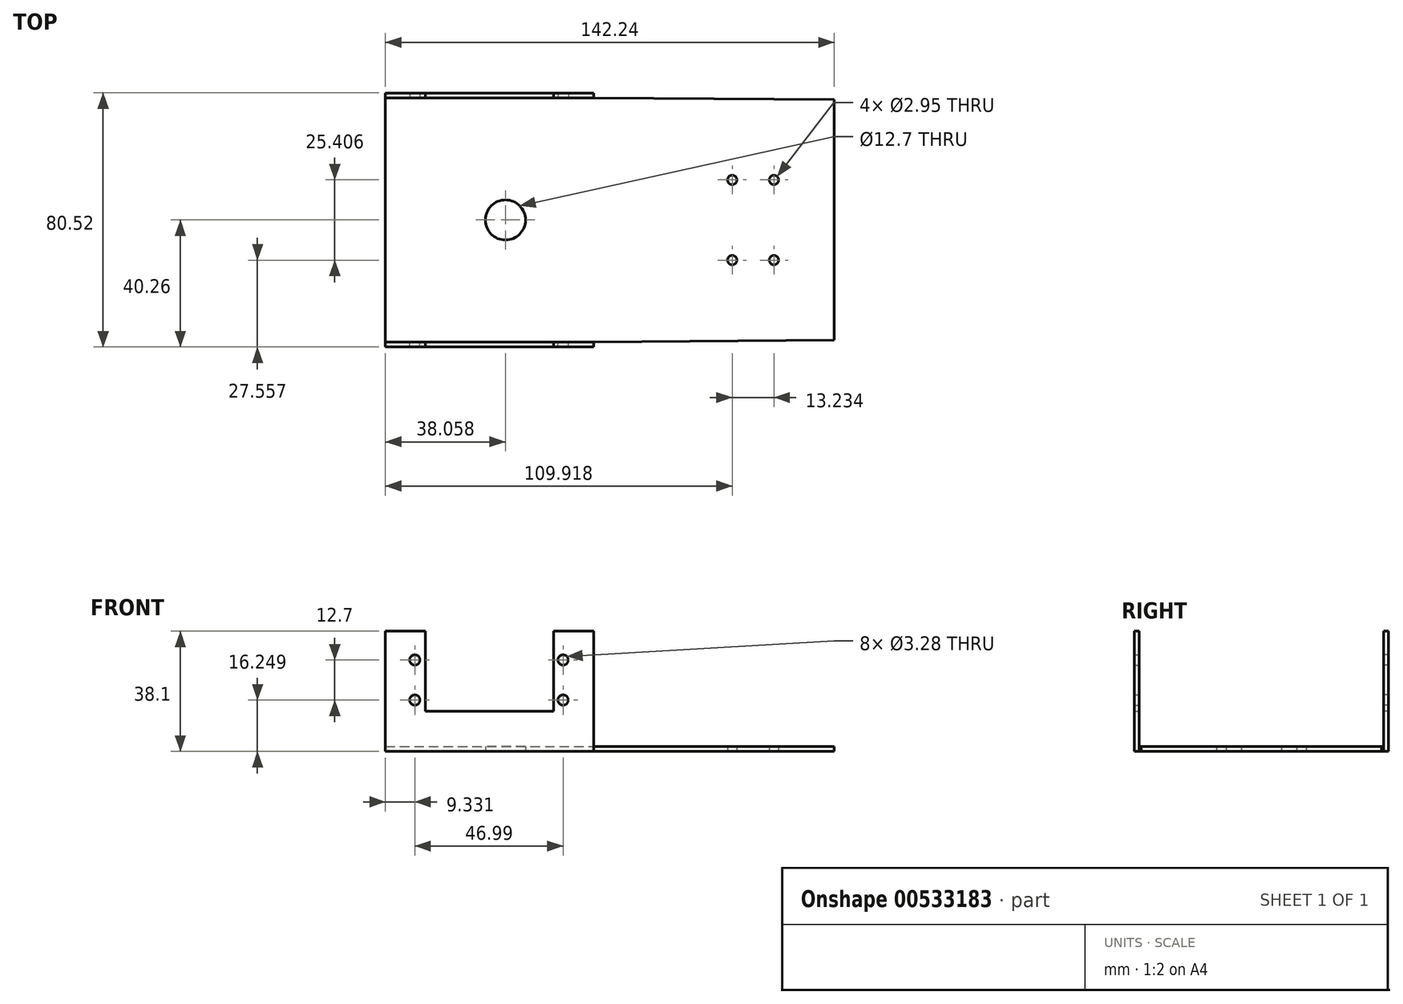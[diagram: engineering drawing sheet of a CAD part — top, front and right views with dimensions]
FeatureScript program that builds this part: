
annotation { "Feature Type Name" : "Feature", "Feature Type Description" : "" }
export const myFeature = defineFeature(function(context is Context, id is Id, definition is map)
    precondition{}
    {
        {
            var Q0;
            Q0=qCreatedBy(makeId("Top.planeOp"),FACE);
            var sketch = newSketch(context, id + "F0", { "sketchPlane" : qUnion([Q0])});
            skLineSegment(sketch, "E0", {"start": v(11.92, 38.1) * mm, "end": v(11.92, 0) * mm});
            skCircle(sketch, "E1", {"center": v(-92.26, 0) * mm, "radius": 6.35 * mm});
            skCircle(sketch, "E2", {"center": v(-20.4, 12.7) * mm, "radius": 1.47 * mm});
            skCircle(sketch, "E3", {"center": v(-7.17, 12.7) * mm, "radius": 1.47 * mm});
            skCircle(sketch, "E4.MirrorC", {"center": v(-20.4, -12.7) * mm, "radius": 1.47 * mm});
            skCircle(sketch, "E5.MirrorC", {"center": v(-7.17, -12.7) * mm, "radius": 1.47 * mm});
            skLineSegment(sketch, "E6.MirrorCS", {"start": v(11.92, -38.1) * mm, "end": v(11.92, 0) * mm});
            skLineSegment(sketch, "E7.MirrorCS", {"start": v(-64.28, -38.1) * mm, "end": v(11.92, -38.1) * mm});
            skLineSegment(sketch, "E8", {"start": v(-64.28, -38.1) * mm, "end": v(-130.32, -37.78) * mm});
            skLineSegment(sketch, "E9", {"start": v(-130.32, 0) * mm, "end": v(-130.32, -37.78) * mm});
            skLineSegment(sketch, "E10", {"start": v(-130.32, 38.73) * mm, "end": v(-130.32, 0) * mm});
            skLineSegment(sketch, "E11", {"start": v(-130.32, 38.73) * mm, "end": v(-64.28, 38.73) * mm});
            skLineSegment(sketch, "E12", {"start": v(-130.32, -37.78) * mm, "end": v(11.92, -38.1) * mm});
            skLineSegment(sketch, "E13", {"start": v(-64.28, 38.73) * mm, "end": v(11.92, 38.1) * mm});
            skSolve(sketch);
        }
        {
            var Q0;
            Q0 = qSketchRegion(id + "F0", true);
            extrude(context, id + "F1", {"entities" : qUnion([Q0]), "depth" : 1.52 * mm, "offsetDistance" : 25.4 * mm});
        }
        {
            var Q0;
            Q0=qCreatedBy(makeId("Top.planeOp"),FACE);
            var sketch = newSketch(context, id + "F2", { "sketchPlane" : qUnion([Q0])});
            skLineSegment(sketch, "E14", {"start": v(-130.32, 38.73) * mm, "end": v(-130.32, 40.26) * mm});
            skLineSegment(sketch, "E15", {"start": v(-130.32, 40.26) * mm, "end": v(-64.28, 40.26) * mm});
            skLineSegment(sketch, "E16", {"start": v(-64.28, 40.26) * mm, "end": v(-64.28, 38.73) * mm});
            skLineSegment(sketch, "E17", {"start": v(-64.28, 38.73) * mm, "end": v(-130.32, 38.73) * mm});
            skSolve(sketch);
        }
        {
            var Q0;
            Q0 = qSketchRegion(id + "F2", true);
            extrude(context, id + "F3", {"entities" : qUnion([Q0]), "operationType" : NewBodyOperationType.ADD, "depth" : 38.1 * mm, "offsetDistance" : 25.4 * mm});
        }
        {
            var Q0;
            Q0=makeQuery(id+"F3.opExtrude","SWEPT_FACE",FACE,{"disambiguationData":[OSD([sQuery(id+"F2.wireOp",EDGE,"E17")])]});
            var sketch = newSketch(context, id + "F4", { "sketchPlane" : qUnion([Q0])});
            skLineSegment(sketch, "E18", {"start": v(-117.62, 38.1) * mm, "end": v(-117.62, 12.7) * mm});
            skLineSegment(sketch, "E19", {"start": v(-117.62, 12.7) * mm, "end": v(-76.98, 12.7) * mm});
            skLineSegment(sketch, "E20", {"start": v(-76.98, 12.7) * mm, "end": v(-76.98, 38.1) * mm});
            skLineSegment(sketch, "E21", {"start": v(-76.98, 38.1) * mm, "end": v(-117.62, 38.1) * mm});
            skCircle(sketch, "E22", {"center": v(-120.99, 28.95) * mm, "radius": 1.64 * mm});
            skCircle(sketch, "E23", {"center": v(-120.99, 16.25) * mm, "radius": 1.64 * mm});
            skCircle(sketch, "E24", {"center": v(-74, 16.25) * mm, "radius": 1.64 * mm});
            skCircle(sketch, "E25", {"center": v(-74, 28.95) * mm, "radius": 1.64 * mm});
            skSolve(sketch);
        }
        {
            var Q0;
            Q0 = qSketchRegion(id + "F4", true);
            extrude(context, id + "F5", {"entities" : qUnion([Q0]), "operationType" : NewBodyOperationType.REMOVE, "oppositeDirection" : true, "depth" : 1.52 * mm, "offsetDistance" : 25.4 * mm});
        }
        {
            var Q0;
            Q0=makeQuery(id+"F1.opExtrude","SWEPT_BODY",BODY,{"disambiguationData":[OSD([sQuery(id+"F0.wireOp",EDGE,"E0"),sQuery(id+"F0.wireOp",EDGE,"E1"),sQuery(id+"F0.wireOp",EDGE,"E2"),sQuery(id+"F0.wireOp",EDGE,"E3"),sQuery(id+"F0.wireOp",EDGE,"E4.MirrorC"),sQuery(id+"F0.wireOp",EDGE,"E5.MirrorC"),sQuery(id+"F0.wireOp",EDGE,"E6.MirrorCS"),sQuery(id+"F0.wireOp",EDGE,"E7.MirrorCS"),sQuery(id+"F0.wireOp",EDGE,"E8"),sQuery(id+"F0.wireOp",EDGE,"E9"),sQuery(id+"F0.wireOp",EDGE,"E10"),sQuery(id+"F0.wireOp",EDGE,"E11"),sQuery(id+"F0.wireOp",EDGE,"E13")])]});
            var Q1;
            Q1=qCreatedBy(makeId("Front.planeOp"),FACE);
            mirror(context, id + "F6", {"operationType" : NewBodyOperationType.ADD, "entities" : qUnion([Q0]), "mirrorPlane" : qUnion([Q1])});
        }
    });
